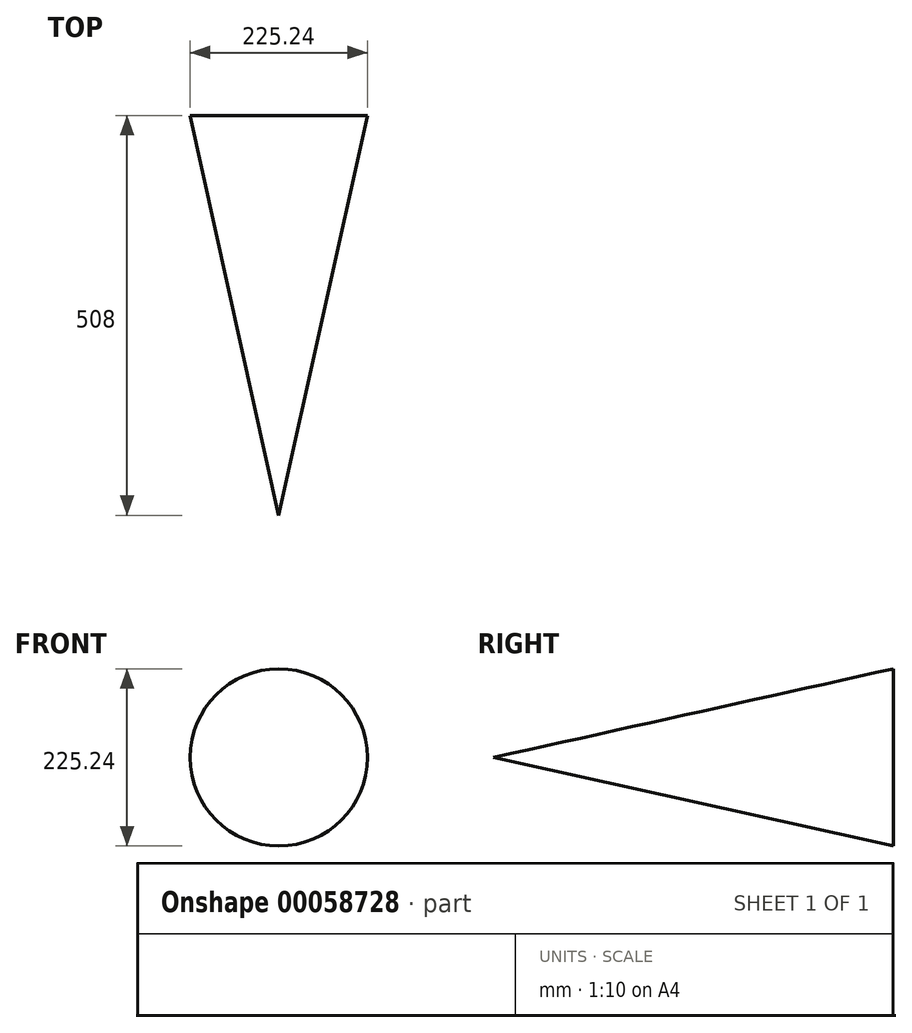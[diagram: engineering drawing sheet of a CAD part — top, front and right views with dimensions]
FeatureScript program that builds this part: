
annotation { "Feature Type Name" : "Feature", "Feature Type Description" : "" }
export const myFeature = defineFeature(function(context is Context, id is Id, definition is map)
    precondition{}
    {
        {
            var Q0;
            Q0=qCreatedBy(makeId("Front.planeOp"),FACE);
            var sketch = newSketch(context, id + "F0", { "sketchPlane" : qUnion([Q0])});
            skCircle(sketch, "E0", {"center": v(0, 0) * mm, "radius": 114.3 * mm});
            skSolve(sketch);
        }
        {
            var Q0;
            Q0=makeQuery(id+"F0.imprint","IMPRINT",FACE,{"disambiguationData":[TD([[makeQuery(id+"F0.imprint","IMPRINT",EDGE,{"derivedFrom":sQuery(id+"F0.wireOp",EDGE,"E0")}),1.0]])]});
            extrude(context, id + "F1", {"entities" : qUnion([Q0]), "depth" : 508 * mm});
        }
        {
            var Q0;
            Q0=makeQuery(id+"F1.opExtrude","CAP_FACE",FACE,{"disambiguationData":[OSD([sQuery(id+"F0.wireOp",EDGE,"E0")])],"isStart":false});
            chamfer(context, id + "F2", {"entities" : qUnion([Q0]), "chamferType" : ChamferType.OFFSET_ANGLE, "width" : 114.3 * mm, "oppositeDirection" : false, "angle" : 77.5 * degree, "tangentPropagation" : true});
        }
    });
